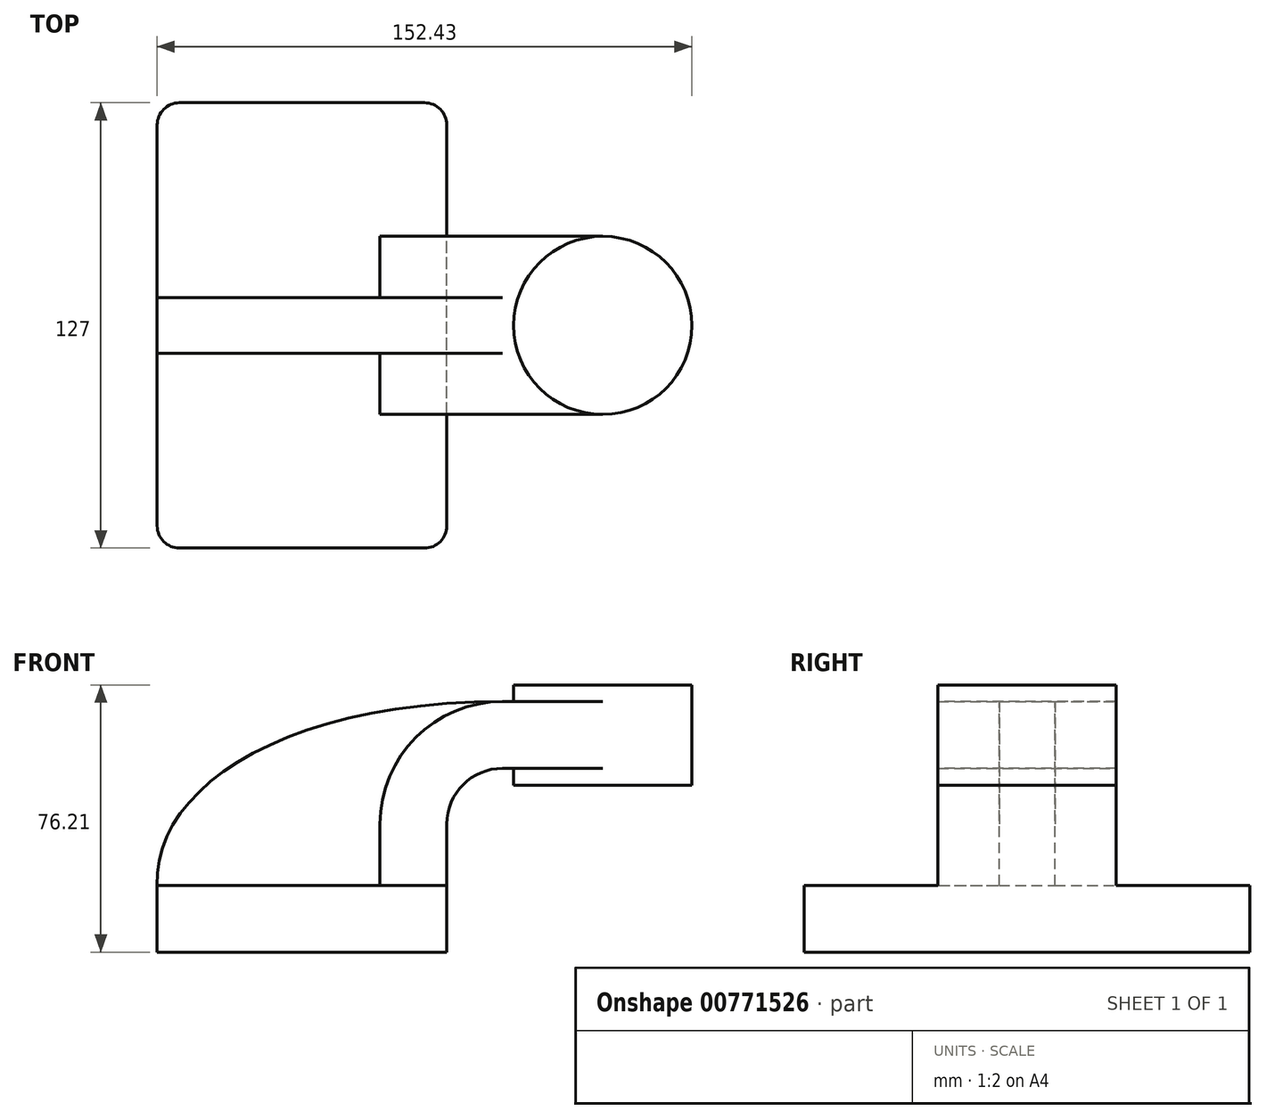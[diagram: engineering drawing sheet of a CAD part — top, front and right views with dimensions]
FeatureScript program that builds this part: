
annotation { "Feature Type Name" : "Feature", "Feature Type Description" : "" }
export const myFeature = defineFeature(function(context is Context, id is Id, definition is map)
    precondition{}
    {
        {
            var Q0;
            Q0=qCreatedBy(makeId("Front.planeOp"),FACE);
            var sketch = newSketch(context, id + "F0", { "sketchPlane" : qUnion([Q0])});
            skLineSegment(sketch, "E0.bottom", {"start": v(-41.28, -9.53) * mm, "end": v(41.28, -9.53) * mm});
            skLineSegment(sketch, "E0.top", {"start": v(-41.28, 9.53) * mm, "end": v(41.28, 9.53) * mm});
            skLineSegment(sketch, "E0.left", {"start": v(-41.28, -9.53) * mm, "end": v(-41.28, 9.53) * mm});
            skLineSegment(sketch, "E0.right", {"start": v(41.28, -9.53) * mm, "end": v(41.28, 9.53) * mm});
            skPoint(sketch, "E0.middle", {"position": v(0, 0) * mm});
            skLineSegment(sketch, "E1.bottom", {"start": v(60.32, 38.1) * mm, "end": v(111.12, 38.1) * mm});
            skLineSegment(sketch, "E1.left", {"start": v(60.32, 38.1) * mm, "end": v(60.32, 66.68) * mm});
            skLineSegment(sketch, "E1.right", {"start": v(111.12, 38.1) * mm, "end": v(111.12, 66.68) * mm});
            skLineSegment(sketch, "E2", {"start": v(41.28, 9.52) * mm, "end": v(41.28, 27) * mm});
            skArc(sketch, "E3", {"start": v(57.15, 42.88) * mm, "mid": v(45.92, 38.23) * mm, "end": v(41.27, 27) * mm});
            skLineSegment(sketch, "E4", {"start": v(57.15, 42.88) * mm, "end": v(85.72, 42.88) * mm});
            skLineSegment(sketch, "E5.0", {"start": v(22.23, 9.52) * mm, "end": v(22.23, 27) * mm});
            skArc(sketch, "E5.1", {"start": v(57.15, 61.93) * mm, "mid": v(32.45, 51.7) * mm, "end": v(22.23, 27) * mm});
            skLineSegment(sketch, "E5.2", {"start": v(57.15, 61.93) * mm, "end": v(85.72, 61.93) * mm});
            skFitSpline(sketch, "E6", {"points": [v(-41.28, 9.53) * mm, v(57.15, 61.93) * mm], "startDerivative": vector(-3.4, 81.58) * mm, "endDerivative": vector(189.65, 0.06) * mm});
            skLineSegment(sketch, "E7", {"start": v(60.32, 66.68) * mm, "end": v(111.12, 66.68) * mm});
            skLineSegment(sketch, "E8", {"start": v(85.72, 66.68) * mm, "end": v(85.72, 42.88) * mm});
            skLineSegment(sketch, "E9", {"start": v(85.72, 66.68) * mm, "end": v(85.72, 38.1) * mm});
            skSolve(sketch);
        }
        {
            var Q0;
            Q0=makeQuery(id+"F0.imprint","IMPRINT",FACE,{"disambiguationData":[TD([[makeQuery(id+"F0.imprint","IMPRINT",EDGE,{"derivedFrom":sQuery(id+"F0.wireOp",EDGE,"E0.bottom")}),1.0]])]});
            extrude(context, id + "F1", {"entities" : qUnion([Q0]), "endBound" : BoundingType.SYMMETRIC, "depth" : 127 * mm, "offsetDistance" : 25.4 * mm});
        }
        {
            var Q0;
            {var subQ1=sQuery(id+"F0.wireOp",EDGE,"E2");Q0=makeQuery(id+"F0.imprint","IMPRINT",FACE,{"disambiguationData":[TD([[makeQuery(id+"F0.imprint","IMPRINT",EDGE,{"derivedFrom":subQ1}),1.0]])]});}
            var Q1;
            {var subQ0=sQuery(id+"F0.wireOp",EDGE,"E4");var subQ1=sQuery(id+"F0.wireOp",EDGE,"E1.left");var subQ2=makeQuery(id+"F0.imprint","INTERSECT",VERTEX,{"derivedFrom":[subQ1,subQ0]});Q1=makeQuery(id+"F0.imprint","IMPRINT",FACE,{"disambiguationData":[TD([[makeQuery(id+"F0.imprint","IMPRINT",EDGE,{"disambiguationData":[TD([[subQ2,-1.0]])],"derivedFrom":subQ1}),-1.0]])]});}
            extrude(context, id + "F2", {"entities" : qUnion([Q0, Q1]), "operationType" : NewBodyOperationType.ADD, "endBound" : BoundingType.SYMMETRIC, "depth" : 50.8 * mm, "offsetDistance" : 25.4 * mm});
        }
        {
            var Q0;
            {var subQ2=sQuery(id+"F0.wireOp",EDGE,"E5.0");Q0=makeQuery(id+"F0.imprint","IMPRINT",FACE,{"disambiguationData":[TD([[makeQuery(id+"F0.imprint","IMPRINT",EDGE,{"derivedFrom":subQ2}),1.0]])]});}
            extrude(context, id + "F3", {"entities" : qUnion([Q0]), "operationType" : NewBodyOperationType.ADD, "endBound" : BoundingType.SYMMETRIC, "depth" : 15.88 * mm, "offsetDistance" : 25.4 * mm});
        }
        {
            var Q0;
            {var subQ4=sQuery(id+"F0.wireOp",EDGE,"E1.right");Q0=makeQuery(id+"F0.imprint","IMPRINT",FACE,{"disambiguationData":[TD([[makeQuery(id+"F0.imprint","IMPRINT",EDGE,{"derivedFrom":subQ4}),1.0]])]});}
            var Q1;
            Q1=sQuery(id+"F0.wireOp",EDGE,"E9");
            revolve(context, id + "F4", {"operationType" : NewBodyOperationType.ADD, "surfaceOperationType" : NewSurfaceOperationType.NEW, "entities" : qUnion([Q0]), "axis" : qUnion([Q1]), "revolveType" : RevolveType.FULL});
        }
        {
            var Q0;
            Q0=makeQuery(id+"F1.opExtrude","CAP_EDGE",EDGE,{"disambiguationData":[OSD([sQuery(id+"F0.wireOp",EDGE,"E0.right")])],"isStart":false});
            var Q1;
            Q1=makeQuery(id+"F1.opExtrude","CAP_EDGE",EDGE,{"disambiguationData":[OSD([sQuery(id+"F0.wireOp",EDGE,"E0.left")])],"isStart":false});
            var Q2;
            Q2=makeQuery(id+"F1.opExtrude","CAP_EDGE",EDGE,{"disambiguationData":[OSD([sQuery(id+"F0.wireOp",EDGE,"E0.left")])],"isStart":true});
            var Q3;
            Q3=makeQuery(id+"F1.opExtrude","CAP_EDGE",EDGE,{"disambiguationData":[OSD([sQuery(id+"F0.wireOp",EDGE,"E0.right")])],"isStart":true});
            fillet(context, id + "F5", {"entities" : qUnion([Q0, Q1, Q2, Q3]), "radius" : 6.35 * mm, "tangentPropagation" : true, "allowEdgeOverflow" : false});
        }
    });
